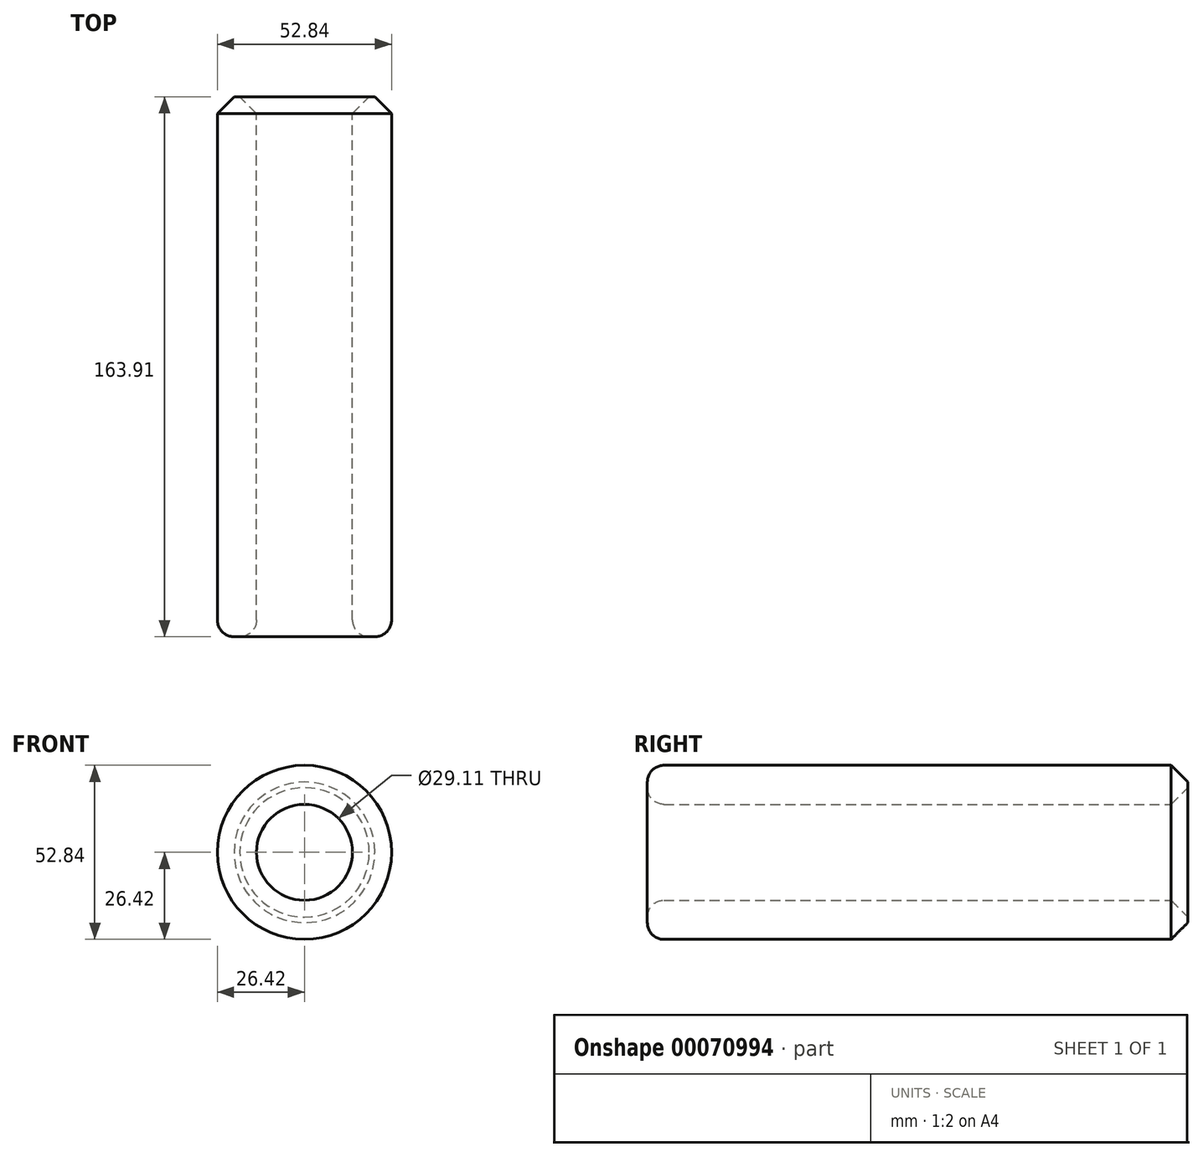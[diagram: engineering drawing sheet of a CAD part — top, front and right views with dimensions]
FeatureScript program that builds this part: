
annotation { "Feature Type Name" : "Feature", "Feature Type Description" : "" }
export const myFeature = defineFeature(function(context is Context, id is Id, definition is map)
    precondition{}
    {
        {
            var Q0;
            Q0=qCreatedBy(makeId("Front.planeOp"),FACE);
            var sketch = newSketch(context, id + "F0", { "sketchPlane" : qUnion([Q0])});
            skCircle(sketch, "E0", {"center": v(0, 0) * mm, "radius": 26.42 * mm});
            skCircle(sketch, "E1", {"center": v(0, 0) * mm, "radius": 14.56 * mm});
            skSolve(sketch);
        }
        {
            var Q0;
            Q0=makeQuery(id+"F0.imprint","IMPRINT",FACE,{"disambiguationData":[TD([[makeQuery(id+"F0.imprint","IMPRINT",EDGE,{"derivedFrom":sQuery(id+"F0.wireOp",EDGE,"E0")}),1.0]])]});
            extrude(context, id + "F1", {"entities" : qUnion([Q0]), "depth" : 163.9 * mm});
        }
        {
            var Q0;
            Q0=makeQuery(id+"F1.opExtrude","CAP_EDGE",EDGE,{"disambiguationData":[OSD([sQuery(id+"F0.wireOp",EDGE,"E0")])],"isStart":false});
            var Q1;
            Q1=makeQuery(id+"F1.opExtrude","CAP_EDGE",EDGE,{"disambiguationData":[OSD([sQuery(id+"F0.wireOp",EDGE,"E1")])],"isStart":false});
            fillet(context, id + "F2", {"entities" : qUnion([Q0, Q1]), "radius" : 5.08 * mm, "tangentPropagation" : true, "allowEdgeOverflow" : false});
        }
        {
            var Q0;
            Q0=makeQuery(id+"F1.opExtrude","CAP_EDGE",EDGE,{"disambiguationData":[OSD([sQuery(id+"F0.wireOp",EDGE,"E0")])],"isStart":true});
            var Q1;
            Q1=makeQuery(id+"F1.opExtrude","CAP_EDGE",EDGE,{"disambiguationData":[OSD([sQuery(id+"F0.wireOp",EDGE,"E1")])],"isStart":true});
            chamfer(context, id + "F3", {"entities" : qUnion([Q0, Q1]), "width" : 5.08 * mm, "tangentPropagation" : true});
        }
    });
